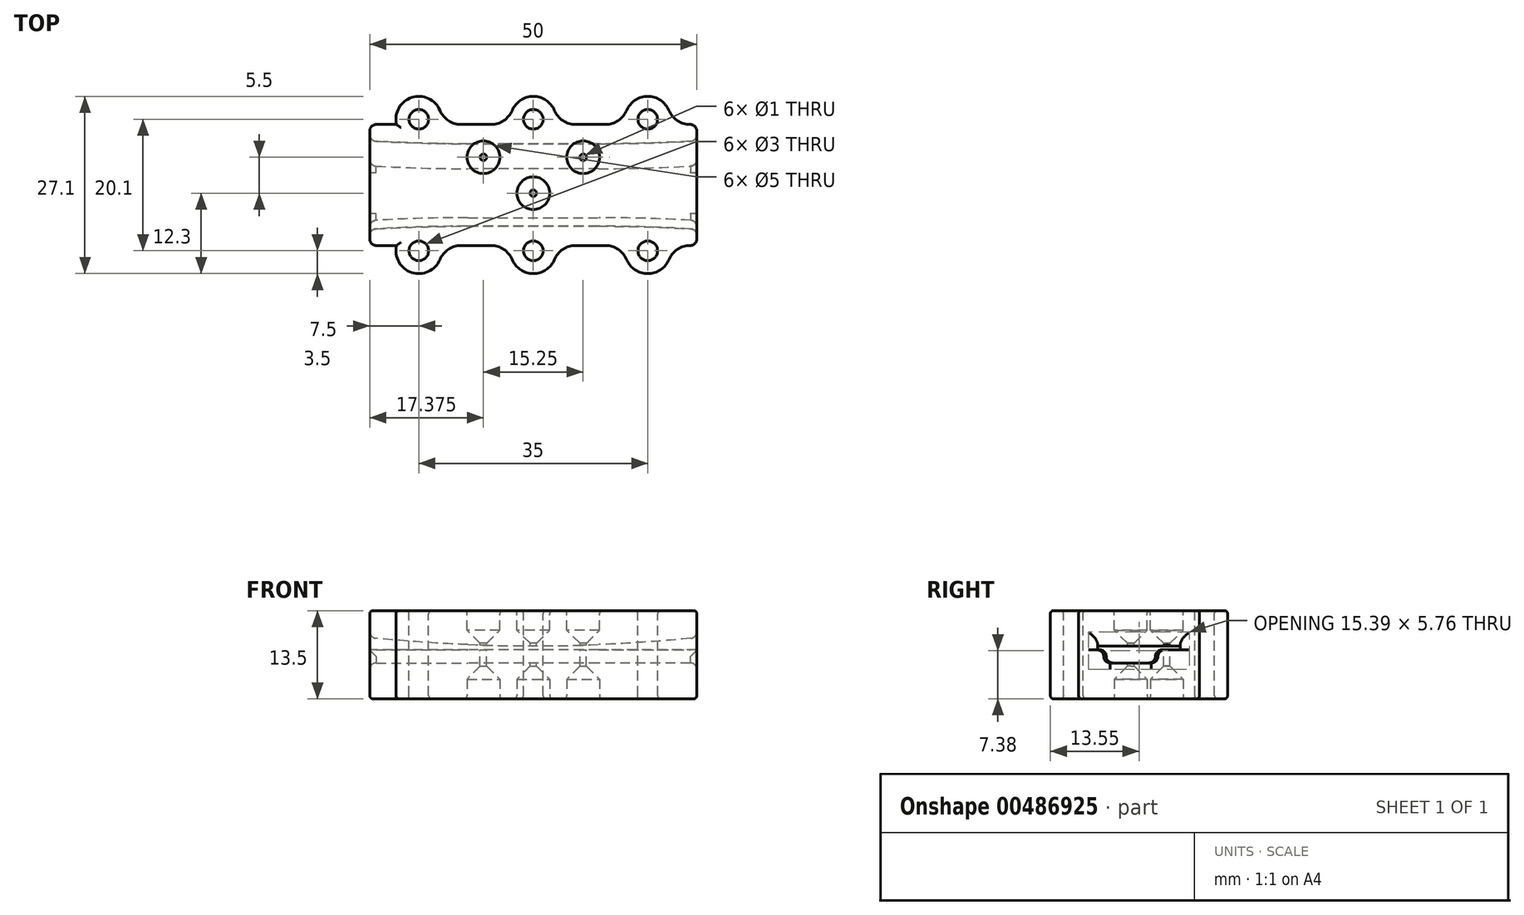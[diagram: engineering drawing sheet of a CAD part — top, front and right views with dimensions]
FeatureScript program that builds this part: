
annotation { "Feature Type Name" : "Feature", "Feature Type Description" : "" }
export const myFeature = defineFeature(function(context is Context, id is Id, definition is map)
    precondition{}
    {
        {
            var Q0;
            Q0=qCreatedBy(makeId("Top.planeOp"),FACE);
            var sketch = newSketch(context, id + "F0", { "sketchPlane" : qUnion([Q0])});
            skLineSegment(sketch, "E0", {"start": v(0, 5) * mm, "end": v(25, 5) * mm});
            skLineSegment(sketch, "E1", {"start": v(0, -4.25) * mm, "end": v(25, -4.25) * mm, "construction": true});
            skArc(sketch, "E2", {"start": v(10, 2.05) * mm, "mid": v(17.5, 2.16) * mm, "end": v(25, 2.5) * mm});
            skPoint(sketch, "E3", {"position": v(0, 2.25) * mm});
            skLineSegment(sketch, "E4", {"start": v(25, 5) * mm, "end": v(25, 2.5) * mm});
            skPoint(sketch, "E5", {"position": v(25, 2.5) * mm});
            skLineSegment(sketch, "E6.MirrorCS", {"start": v(0, 5) * mm, "end": v(-25, 5) * mm});
            skLineSegment(sketch, "E7.MirrorCS", {"start": v(-25, 5) * mm, "end": v(-25, 2.5) * mm});
            skLineSegment(sketch, "E8.MirrorCS", {"start": v(25, -13.5) * mm, "end": v(25, -11) * mm});
            skLineSegment(sketch, "E9.MirrorCS", {"start": v(0, -13.5) * mm, "end": v(25, -13.5) * mm});
            skLineSegment(sketch, "E10.MirrorCS", {"start": v(0, -13.5) * mm, "end": v(-25, -13.5) * mm});
            skLineSegment(sketch, "E11.MirrorCS", {"start": v(-25, -13.5) * mm, "end": v(-25, -11) * mm});
            skPoint(sketch, "E12", {"position": v(10, 2.05) * mm});
            skLineSegment(sketch, "E13", {"start": v(0, 2.05) * mm, "end": v(10, 2.05) * mm});
            skLineSegment(sketch, "E14.MirrorCS", {"start": v(0, 2.05) * mm, "end": v(-10, 2.05) * mm});
            skArc(sketch, "E15.MirrorCS", {"start": v(-10, 2.05) * mm, "mid": v(-17.5, 2.16) * mm, "end": v(-25, 2.5) * mm});
            skArc(sketch, "E16.MirrorCS", {"start": v(10, -10.55) * mm, "mid": v(17.5, -10.66) * mm, "end": v(25, -11) * mm});
            skLineSegment(sketch, "E17.MirrorCS", {"start": v(0, -10.55) * mm, "end": v(10, -10.55) * mm});
            skLineSegment(sketch, "E18.MirrorCS", {"start": v(0, -10.55) * mm, "end": v(-10, -10.55) * mm});
            skArc(sketch, "E19.MirrorCS", {"start": v(-10, -10.55) * mm, "mid": v(-17.5, -10.66) * mm, "end": v(-25, -11) * mm});
            skLineSegment(sketch, "E20", {"start": v(0, 1.75) * mm, "end": v(25, 1.75) * mm, "construction": true});
            skLineSegment(sketch, "E21", {"start": v(0, -10.25) * mm, "end": v(25, -10.25) * mm, "construction": true});
            skLineSegment(sketch, "E22", {"start": v(25, -10.25) * mm, "end": v(25, -4.25) * mm, "construction": true});
            skLineSegment(sketch, "E23", {"start": v(25, 1.75) * mm, "end": v(25, -4.25) * mm, "construction": true});
            skLineSegment(sketch, "E24", {"start": v(0, -5.5) * mm, "end": v(25, -5.5) * mm, "construction": true});
            skSolve(sketch);
        }
        {
            var Q0;
            Q0=makeQuery(id+"F0.imprint","IMPRINT",FACE,{"disambiguationData":[TD([[makeQuery(id+"F0.imprint","IMPRINT",EDGE,{"derivedFrom":sQuery(id+"F0.wireOp",EDGE,"E0")}),-1.0]])]});
            var Q1;
            Q1=makeQuery(id+"F0.imprint","IMPRINT",FACE,{"disambiguationData":[TD([[makeQuery(id+"F0.imprint","IMPRINT",EDGE,{"derivedFrom":sQuery(id+"F0.wireOp",EDGE,"E8.MirrorCS")}),1.0]])]});
            extrude(context, id + "F1", {"entities" : qUnion([Q0, Q1]), "depth" : 6 * mm});
        }
        {
            var Q0;
            Q0=makeQuery(id+"F1.opExtrude","SWEPT_FACE",FACE,{"disambiguationData":[OSD([sQuery(id+"F0.wireOp",EDGE,"E9.MirrorCS"),sQuery(id+"F0.wireOp",EDGE,"E10.MirrorCS")])]});
            var sketch = newSketch(context, id + "F2", { "sketchPlane" : qUnion([Q0])});
            skLineSegment(sketch, "E25", {"start": v(0, 6) * mm, "end": v(25, 6) * mm});
            skLineSegment(sketch, "E26", {"start": v(25, 6) * mm, "end": v(25, 1.85) * mm});
            skArc(sketch, "E27", {"start": v(0, 0.6) * mm, "mid": v(12.52, 0.91) * mm, "end": v(25, 1.85) * mm});
            skPoint(sketch, "E28", {"position": v(25, 1.85) * mm});
            skPoint(sketch, "E29", {"position": v(0, 0.6) * mm});
            skLineSegment(sketch, "E30.MirrorCS", {"start": v(0, 6) * mm, "end": v(-25, 6) * mm});
            skLineSegment(sketch, "E31.MirrorCS", {"start": v(-25, 6) * mm, "end": v(-25, 1.85) * mm});
            skArc(sketch, "E32.MirrorCS", {"start": v(0, 0.6) * mm, "mid": v(-12.52, 0.91) * mm, "end": v(-25, 1.85) * mm});
            skSolve(sketch);
        }
        {
            var Q0;
            Q0 = qSketchRegion(id + "F2", true);
            var Q1;
            Q1=makeQuery(id+"F1.opExtrude","SWEPT_FACE",FACE,{"disambiguationData":[OSD([sQuery(id+"F0.wireOp",EDGE,"E0"),sQuery(id+"F0.wireOp",EDGE,"9c2fb416-197e-4b27-b734-f3fda417422a0.MirrorCS")])]});
            extrude(context, id + "F3", {"entities" : qUnion([Q0]), "operationType" : NewBodyOperationType.ADD, "endBound" : BoundingType.UP_TO_SURFACE, "oppositeDirection" : true, "endBoundEntityFace" : qUnion([Q1]), "depth" : 25 * mm});
        }
        {
            var Q0;
            Q0=makeQuery(id+"F1.opExtrude","CAP_FACE",FACE,{"disambiguationData":[OSD([sQuery(id+"F0.wireOp",EDGE,"E8.MirrorCS"),sQuery(id+"F0.wireOp",EDGE,"E9.MirrorCS"),sQuery(id+"F0.wireOp",EDGE,"E10.MirrorCS"),sQuery(id+"F0.wireOp",EDGE,"E11.MirrorCS"),sQuery(id+"F0.wireOp",EDGE,"E16.MirrorCS"),sQuery(id+"F0.wireOp",EDGE,"E17.MirrorCS"),sQuery(id+"F0.wireOp",EDGE,"E18.MirrorCS"),sQuery(id+"F0.wireOp",EDGE,"E19.MirrorCS")])],"isStart":true});
            var sketch = newSketch(context, id + "F4", { "sketchPlane" : qUnion([Q0])});
            skLineSegment(sketch, "E33", {"start": v(-10, 9.25) * mm, "end": v(10, 9.25) * mm});
            skLineSegment(sketch, "E34", {"start": v(-25, 13.5) * mm, "end": v(25, 13.5) * mm});
            skArc(sketch, "E35", {"start": v(-25, 9.7) * mm, "mid": v(-17.5, 9.36) * mm, "end": v(-10, 9.25) * mm});
            skLineSegment(sketch, "E36", {"start": v(-25, 13.5) * mm, "end": v(-25, 9.7) * mm});
            skArc(sketch, "E37.MirrorCS", {"start": v(25, 9.7) * mm, "mid": v(17.5, 9.36) * mm, "end": v(10, 9.25) * mm});
            skLineSegment(sketch, "E38.MirrorCS", {"start": v(25, 13.5) * mm, "end": v(25, 9.7) * mm});
            skLineSegment(sketch, "E39", {"start": v(-25, 1.3) * mm, "end": v(-25, -5) * mm});
            skLineSegment(sketch, "E40", {"start": v(-25, -5) * mm, "end": v(25, -5) * mm});
            skLineSegment(sketch, "E41", {"start": v(25, -5) * mm, "end": v(25, 1.3) * mm});
            skArc(sketch, "E42.MirrorCS", {"start": v(25, 1.3) * mm, "mid": v(17.5, 1.64) * mm, "end": v(10, 1.75) * mm});
            skLineSegment(sketch, "E43.MirrorCS", {"start": v(-10, 1.75) * mm, "end": v(10, 1.75) * mm});
            skArc(sketch, "E44.MirrorCS", {"start": v(-25, 1.3) * mm, "mid": v(-17.5, 1.64) * mm, "end": v(-10, 1.75) * mm});
            skSolve(sketch);
        }
        {
            var Q0;
            Q0 = qSketchRegion(id + "F4", true);
            extrude(context, id + "F5", {"entities" : qUnion([Q0]), "depth" : 7.5 * mm});
        }
        {
            var Q0;
            Q0=makeQuery(id+"F5.opExtrude","SWEPT_FACE",FACE,{"disambiguationData":[OSD([sQuery(id+"F4.wireOp",EDGE,"E34")])]});
            var sketch = newSketch(context, id + "F6", { "sketchPlane" : qUnion([Q0])});
            skPoint(sketch, "E45", {"position": v(-25, -2) * mm});
            skPoint(sketch, "E46", {"position": v(25, -2) * mm});
            skLineSegment(sketch, "E47", {"start": v(-25, -2) * mm, "end": v(-25, -7.5) * mm});
            skLineSegment(sketch, "E48", {"start": v(-25, -7.5) * mm, "end": v(25, -7.5) * mm});
            skLineSegment(sketch, "E49", {"start": v(25, -7.5) * mm, "end": v(25, -2) * mm});
            skLineSegment(sketch, "E50", {"start": v(25, -2) * mm, "end": v(-25, -2) * mm});
            skSolve(sketch);
        }
        {
            var Q0;
            Q0 = qSketchRegion(id + "F6", true);
            var Q1;
            Q1=makeQuery(id+"F5.opExtrude","SWEPT_FACE",FACE,{"disambiguationData":[OSD([sQuery(id+"F4.wireOp",EDGE,"E40")])]});
            extrude(context, id + "F7", {"entities" : qUnion([Q0]), "operationType" : NewBodyOperationType.ADD, "endBound" : BoundingType.UP_TO_SURFACE, "oppositeDirection" : true, "endBoundEntityFace" : qUnion([Q1]), "depth" : 25 * mm});
        }
        {
            var Q0;
            Q0=makeQuery(id+"F3.boolean.opBoolean","MERGE",FACE,{"derivedFrom":[makeQuery(id+"F1.opExtrude","CAP_FACE",FACE,{"disambiguationData":[OSD([sQuery(id+"F0.wireOp",EDGE,"E0"),sQuery(id+"F0.wireOp",EDGE,"E2"),sQuery(id+"F0.wireOp",EDGE,"E4"),sQuery(id+"F0.wireOp",EDGE,"E6.MirrorCS"),sQuery(id+"F0.wireOp",EDGE,"E7.MirrorCS"),sQuery(id+"F0.wireOp",EDGE,"E13"),sQuery(id+"F0.wireOp",EDGE,"E14.MirrorCS"),sQuery(id+"F0.wireOp",EDGE,"E15.MirrorCS")])],"isStart":false}),makeQuery(id+"F1.opExtrude","CAP_FACE",FACE,{"disambiguationData":[OSD([sQuery(id+"F0.wireOp",EDGE,"E8.MirrorCS"),sQuery(id+"F0.wireOp",EDGE,"E9.MirrorCS"),sQuery(id+"F0.wireOp",EDGE,"E10.MirrorCS"),sQuery(id+"F0.wireOp",EDGE,"E11.MirrorCS"),sQuery(id+"F0.wireOp",EDGE,"E16.MirrorCS"),sQuery(id+"F0.wireOp",EDGE,"E17.MirrorCS"),sQuery(id+"F0.wireOp",EDGE,"E18.MirrorCS"),sQuery(id+"F0.wireOp",EDGE,"E19.MirrorCS")])],"isStart":false}),makeQuery(id+"F3.opExtrude","SWEPT_FACE",FACE,{"disambiguationData":[OSD([sQuery(id+"F2.wireOp",EDGE,"E25"),sQuery(id+"F2.wireOp",EDGE,"E30.MirrorCS")])]})]});
            var sketch = newSketch(context, id + "F8", { "sketchPlane" : qUnion([Q0])});
            skArc(sketch, "E51", {"start": v(14.1, -13.5) * mm, "mid": v(17.5, -17.8) * mm, "end": v(20.9, -13.5) * mm});
            skArc(sketch, "E52", {"start": v(20.9, 5) * mm, "mid": v(17.5, 9.3) * mm, "end": v(14.1, 5) * mm});
            skLineSegment(sketch, "E53", {"start": v(20.9, -13.5) * mm, "end": v(14.1, -13.5) * mm});
            skLineSegment(sketch, "E54", {"start": v(20.9, 5) * mm, "end": v(14.1, 5) * mm});
            skArc(sketch, "E55.MirrorCS", {"start": v(-14.1, -13.5) * mm, "mid": v(-17.5, -17.8) * mm, "end": v(-20.9, -13.5) * mm});
            skArc(sketch, "E56.MirrorCS", {"start": v(-20.9, 5) * mm, "mid": v(-17.5, 9.3) * mm, "end": v(-14.1, 5) * mm});
            skLineSegment(sketch, "E57.MirrorCS", {"start": v(-20.9, 5) * mm, "end": v(-14.1, 5) * mm});
            skLineSegment(sketch, "E58.MirrorCS", {"start": v(-20.9, -13.5) * mm, "end": v(-14.1, -13.5) * mm});
            skArc(sketch, "E59", {"start": v(3.4, 5) * mm, "mid": v(0, 9.3) * mm, "end": v(-3.4, 5) * mm});
            skArc(sketch, "E60", {"start": v(-3.4, -13.5) * mm, "mid": v(0, -17.8) * mm, "end": v(3.4, -13.5) * mm});
            skLineSegment(sketch, "E61", {"start": v(-3.4, 5) * mm, "end": v(3.4, 5) * mm});
            skLineSegment(sketch, "E62", {"start": v(-3.4, -13.5) * mm, "end": v(3.4, -13.5) * mm});
            skSolve(sketch);
        }
        {
            var Q0;
            Q0 = qSketchRegion(id + "F8", true);
            var Q1;
            Q1=makeQuery(id+"F1.opExtrude","CAP_FACE",FACE,{"disambiguationData":[OSD([sQuery(id+"F0.wireOp",EDGE,"E8.MirrorCS"),sQuery(id+"F0.wireOp",EDGE,"E9.MirrorCS"),sQuery(id+"F0.wireOp",EDGE,"E10.MirrorCS"),sQuery(id+"F0.wireOp",EDGE,"E11.MirrorCS"),sQuery(id+"F0.wireOp",EDGE,"E16.MirrorCS"),sQuery(id+"F0.wireOp",EDGE,"E17.MirrorCS"),sQuery(id+"F0.wireOp",EDGE,"E18.MirrorCS"),sQuery(id+"F0.wireOp",EDGE,"E19.MirrorCS")])],"isStart":true});
            extrude(context, id + "F9", {"entities" : qUnion([Q0]), "operationType" : NewBodyOperationType.ADD, "endBound" : BoundingType.UP_TO_SURFACE, "oppositeDirection" : true, "endBoundEntityFace" : qUnion([Q1]), "depth" : 25 * mm});
        }
        {
            var Q0;
            Q0=makeQuery(id+"F7.boolean.opBoolean","MERGE",FACE,{"derivedFrom":[makeQuery(id+"F5.opExtrude","CAP_FACE",FACE,{"disambiguationData":[OSD([sQuery(id+"F4.wireOp",EDGE,"E33"),sQuery(id+"F4.wireOp",EDGE,"E34"),sQuery(id+"F4.wireOp",EDGE,"E35"),sQuery(id+"F4.wireOp",EDGE,"E36"),sQuery(id+"F4.wireOp",EDGE,"E37.MirrorCS"),sQuery(id+"F4.wireOp",EDGE,"E38.MirrorCS")])],"isStart":false}),makeQuery(id+"F5.opExtrude","CAP_FACE",FACE,{"disambiguationData":[OSD([sQuery(id+"F4.wireOp",EDGE,"E39"),sQuery(id+"F4.wireOp",EDGE,"E40"),sQuery(id+"F4.wireOp",EDGE,"E41"),sQuery(id+"F4.wireOp",EDGE,"E42.MirrorCS"),sQuery(id+"F4.wireOp",EDGE,"E43.MirrorCS"),sQuery(id+"F4.wireOp",EDGE,"E44.MirrorCS")])],"isStart":false}),makeQuery(id+"F7.opExtrude","SWEPT_FACE",FACE,{"disambiguationData":[OSD([sQuery(id+"F6.wireOp",EDGE,"E48")])]})]});
            var sketch = newSketch(context, id + "F10", { "sketchPlane" : qUnion([Q0])});
            skArc(sketch, "E63", {"start": v(-14.1, 13.5) * mm, "mid": v(-17.5, 17.8) * mm, "end": v(-20.9, 13.5) * mm});
            skArc(sketch, "E64", {"start": v(-20.9, -5) * mm, "mid": v(-17.5, -9.3) * mm, "end": v(-14.1, -5) * mm});
            skLineSegment(sketch, "E65", {"start": v(-20.9, 13.5) * mm, "end": v(-14.1, 13.5) * mm});
            skLineSegment(sketch, "E66", {"start": v(-20.9, -5) * mm, "end": v(-14.1, -5) * mm});
            skArc(sketch, "E67.MirrorCS", {"start": v(14.1, 13.5) * mm, "mid": v(17.5, 17.8) * mm, "end": v(20.9, 13.5) * mm});
            skLineSegment(sketch, "E68.MirrorCS", {"start": v(20.9, 13.5) * mm, "end": v(14.1, 13.5) * mm});
            skLineSegment(sketch, "E69.MirrorCS", {"start": v(20.9, -5) * mm, "end": v(14.1, -5) * mm});
            skArc(sketch, "E70.MirrorCS", {"start": v(20.9, -5) * mm, "mid": v(17.5, -9.3) * mm, "end": v(14.1, -5) * mm});
            skArc(sketch, "E71", {"start": v(-3.4, -5) * mm, "mid": v(0, -9.3) * mm, "end": v(3.4, -5) * mm});
            skArc(sketch, "E72", {"start": v(3.4, 13.5) * mm, "mid": v(0, 17.8) * mm, "end": v(-3.4, 13.5) * mm});
            skLineSegment(sketch, "E73", {"start": v(3.4, -5) * mm, "end": v(-3.4, -5) * mm});
            skLineSegment(sketch, "E74", {"start": v(3.4, 13.5) * mm, "end": v(-3.4, 13.5) * mm});
            skSolve(sketch);
        }
        {
            var Q0;
            Q0 = qSketchRegion(id + "F10", true);
            var Q1;
            Q1=makeQuery(id+"F5.opExtrude","CAP_FACE",FACE,{"disambiguationData":[OSD([sQuery(id+"F4.wireOp",EDGE,"E33"),sQuery(id+"F4.wireOp",EDGE,"E34"),sQuery(id+"F4.wireOp",EDGE,"E35"),sQuery(id+"F4.wireOp",EDGE,"E36"),sQuery(id+"F4.wireOp",EDGE,"E37.MirrorCS"),sQuery(id+"F4.wireOp",EDGE,"E38.MirrorCS")])],"isStart":true});
            extrude(context, id + "F11", {"entities" : qUnion([Q0]), "operationType" : NewBodyOperationType.ADD, "endBound" : BoundingType.UP_TO_SURFACE, "oppositeDirection" : true, "endBoundEntityFace" : qUnion([Q1]), "depth" : 25 * mm});
        }
        {
            var Q0;
            Q0=makeQuery(id+"F9.boolean.opBoolean","MERGE",FACE,{"derivedFrom":[makeQuery(id+"F3.boolean.opBoolean","MERGE",FACE,{"derivedFrom":[makeQuery(id+"F1.opExtrude","CAP_FACE",FACE,{"disambiguationData":[OSD([sQuery(id+"F0.wireOp",EDGE,"E0"),sQuery(id+"F0.wireOp",EDGE,"E2"),sQuery(id+"F0.wireOp",EDGE,"E4"),sQuery(id+"F0.wireOp",EDGE,"E6.MirrorCS"),sQuery(id+"F0.wireOp",EDGE,"E7.MirrorCS"),sQuery(id+"F0.wireOp",EDGE,"E13"),sQuery(id+"F0.wireOp",EDGE,"E14.MirrorCS"),sQuery(id+"F0.wireOp",EDGE,"E15.MirrorCS")])],"isStart":false}),makeQuery(id+"F1.opExtrude","CAP_FACE",FACE,{"disambiguationData":[OSD([sQuery(id+"F0.wireOp",EDGE,"E8.MirrorCS"),sQuery(id+"F0.wireOp",EDGE,"E9.MirrorCS"),sQuery(id+"F0.wireOp",EDGE,"E10.MirrorCS"),sQuery(id+"F0.wireOp",EDGE,"E11.MirrorCS"),sQuery(id+"F0.wireOp",EDGE,"E16.MirrorCS"),sQuery(id+"F0.wireOp",EDGE,"E17.MirrorCS"),sQuery(id+"F0.wireOp",EDGE,"E18.MirrorCS"),sQuery(id+"F0.wireOp",EDGE,"E19.MirrorCS")])],"isStart":false}),makeQuery(id+"F3.opExtrude","SWEPT_FACE",FACE,{"disambiguationData":[OSD([sQuery(id+"F2.wireOp",EDGE,"E25"),sQuery(id+"F2.wireOp",EDGE,"E30.MirrorCS")])]})]}),makeQuery(id+"F9.opExtrude","CAP_FACE",FACE,{"disambiguationData":[OSD([sQuery(id+"F8.wireOp",EDGE,"E51"),sQuery(id+"F8.wireOp",EDGE,"E53")])],"isStart":true}),makeQuery(id+"F9.opExtrude","CAP_FACE",FACE,{"disambiguationData":[OSD([sQuery(id+"F8.wireOp",EDGE,"E52"),sQuery(id+"F8.wireOp",EDGE,"E54")])],"isStart":true}),makeQuery(id+"F9.opExtrude","CAP_FACE",FACE,{"disambiguationData":[OSD([sQuery(id+"F8.wireOp",EDGE,"E55.MirrorCS"),sQuery(id+"F8.wireOp",EDGE,"E58.MirrorCS")])],"isStart":true}),makeQuery(id+"F9.opExtrude","CAP_FACE",FACE,{"disambiguationData":[OSD([sQuery(id+"F8.wireOp",EDGE,"E56.MirrorCS"),sQuery(id+"F8.wireOp",EDGE,"E57.MirrorCS")])],"isStart":true}),makeQuery(id+"F9.opExtrude","CAP_FACE",FACE,{"disambiguationData":[OSD([sQuery(id+"F8.wireOp",EDGE,"E59"),sQuery(id+"F8.wireOp",EDGE,"E61")])],"isStart":true}),makeQuery(id+"F9.opExtrude","CAP_FACE",FACE,{"disambiguationData":[OSD([sQuery(id+"F8.wireOp",EDGE,"E60"),sQuery(id+"F8.wireOp",EDGE,"E62")])],"isStart":true})]});
            var sketch = newSketch(context, id + "F12", { "sketchPlane" : qUnion([Q0])});
            skCircle(sketch, "E75", {"center": v(-7.62, 0) * mm, "radius": 0.5 * mm});
            skCircle(sketch, "E76.MirrorC", {"center": v(7.62, 0) * mm, "radius": 0.5 * mm});
            skCircle(sketch, "E77", {"center": v(0, -5.5) * mm, "radius": 0.5 * mm});
            skCircle(sketch, "E78", {"center": v(-17.5, 5.8) * mm, "radius": 1.5 * mm});
            skCircle(sketch, "E79", {"center": v(-17.5, -14.3) * mm, "radius": 1.5 * mm});
            skCircle(sketch, "E80.MirrorC", {"center": v(17.5, -14.3) * mm, "radius": 1.5 * mm});
            skCircle(sketch, "E81.MirrorC", {"center": v(17.5, 5.8) * mm, "radius": 1.5 * mm});
            skCircle(sketch, "E82", {"center": v(0, 5.8) * mm, "radius": 1.5 * mm});
            skCircle(sketch, "E83", {"center": v(0, -14.3) * mm, "radius": 1.5 * mm});
            skSolve(sketch);
        }
        {
            var Q0;
            Q0 = qSketchRegion(id + "F12", true);
            extrude(context, id + "F13", {"entities" : qUnion([Q0]), "operationType" : NewBodyOperationType.REMOVE, "endBound" : BoundingType.THROUGH_ALL, "oppositeDirection" : true, "depth" : 25 * mm});
        }
        {
            var Q0;
            Q0=makeQuery(id+"F9.boolean.opBoolean","MERGE",FACE,{"derivedFrom":[makeQuery(id+"F3.boolean.opBoolean","MERGE",FACE,{"derivedFrom":[makeQuery(id+"F1.opExtrude","CAP_FACE",FACE,{"disambiguationData":[OSD([sQuery(id+"F0.wireOp",EDGE,"E0"),sQuery(id+"F0.wireOp",EDGE,"E2"),sQuery(id+"F0.wireOp",EDGE,"E4"),sQuery(id+"F0.wireOp",EDGE,"E6.MirrorCS"),sQuery(id+"F0.wireOp",EDGE,"E7.MirrorCS"),sQuery(id+"F0.wireOp",EDGE,"E13"),sQuery(id+"F0.wireOp",EDGE,"E14.MirrorCS"),sQuery(id+"F0.wireOp",EDGE,"E15.MirrorCS")])],"isStart":false}),makeQuery(id+"F1.opExtrude","CAP_FACE",FACE,{"disambiguationData":[OSD([sQuery(id+"F0.wireOp",EDGE,"E8.MirrorCS"),sQuery(id+"F0.wireOp",EDGE,"E9.MirrorCS"),sQuery(id+"F0.wireOp",EDGE,"E10.MirrorCS"),sQuery(id+"F0.wireOp",EDGE,"E11.MirrorCS"),sQuery(id+"F0.wireOp",EDGE,"E16.MirrorCS"),sQuery(id+"F0.wireOp",EDGE,"E17.MirrorCS"),sQuery(id+"F0.wireOp",EDGE,"E18.MirrorCS"),sQuery(id+"F0.wireOp",EDGE,"E19.MirrorCS")])],"isStart":false}),makeQuery(id+"F3.opExtrude","SWEPT_FACE",FACE,{"disambiguationData":[OSD([sQuery(id+"F2.wireOp",EDGE,"E25"),sQuery(id+"F2.wireOp",EDGE,"E30.MirrorCS")])]})]}),makeQuery(id+"F9.opExtrude","CAP_FACE",FACE,{"disambiguationData":[OSD([sQuery(id+"F8.wireOp",EDGE,"E51"),sQuery(id+"F8.wireOp",EDGE,"E53")])],"isStart":true}),makeQuery(id+"F9.opExtrude","CAP_FACE",FACE,{"disambiguationData":[OSD([sQuery(id+"F8.wireOp",EDGE,"E52"),sQuery(id+"F8.wireOp",EDGE,"E54")])],"isStart":true}),makeQuery(id+"F9.opExtrude","CAP_FACE",FACE,{"disambiguationData":[OSD([sQuery(id+"F8.wireOp",EDGE,"E55.MirrorCS"),sQuery(id+"F8.wireOp",EDGE,"E58.MirrorCS")])],"isStart":true}),makeQuery(id+"F9.opExtrude","CAP_FACE",FACE,{"disambiguationData":[OSD([sQuery(id+"F8.wireOp",EDGE,"E56.MirrorCS"),sQuery(id+"F8.wireOp",EDGE,"E57.MirrorCS")])],"isStart":true}),makeQuery(id+"F9.opExtrude","CAP_FACE",FACE,{"disambiguationData":[OSD([sQuery(id+"F8.wireOp",EDGE,"E59"),sQuery(id+"F8.wireOp",EDGE,"E61")])],"isStart":true}),makeQuery(id+"F9.opExtrude","CAP_FACE",FACE,{"disambiguationData":[OSD([sQuery(id+"F8.wireOp",EDGE,"E60"),sQuery(id+"F8.wireOp",EDGE,"E62")])],"isStart":true})]});
            var sketch = newSketch(context, id + "F14", { "sketchPlane" : qUnion([Q0])});
            skCircle(sketch, "E84", {"center": v(-7.62, 0) * mm, "radius": 2.5 * mm});
            skCircle(sketch, "E85", {"center": v(7.62, 0) * mm, "radius": 2.5 * mm});
            skCircle(sketch, "E86", {"center": v(0, -5.5) * mm, "radius": 2.5 * mm});
            skSolve(sketch);
        }
        {
            var Q0;
            Q0 = qSketchRegion(id + "F14", true);
            extrude(context, id + "F15", {"entities" : qUnion([Q0]), "operationType" : NewBodyOperationType.REMOVE, "oppositeDirection" : true, "depth" : 5 * mm});
        }
        {
            var Q0;
            Q0=makeQuery(id+"F11.boolean.opBoolean","MERGE",FACE,{"derivedFrom":[makeQuery(id+"F7.boolean.opBoolean","MERGE",FACE,{"derivedFrom":[makeQuery(id+"F5.opExtrude","CAP_FACE",FACE,{"disambiguationData":[OSD([sQuery(id+"F4.wireOp",EDGE,"E33"),sQuery(id+"F4.wireOp",EDGE,"E34"),sQuery(id+"F4.wireOp",EDGE,"E35"),sQuery(id+"F4.wireOp",EDGE,"E36"),sQuery(id+"F4.wireOp",EDGE,"E37.MirrorCS"),sQuery(id+"F4.wireOp",EDGE,"E38.MirrorCS")])],"isStart":false}),makeQuery(id+"F5.opExtrude","CAP_FACE",FACE,{"disambiguationData":[OSD([sQuery(id+"F4.wireOp",EDGE,"E39"),sQuery(id+"F4.wireOp",EDGE,"E40"),sQuery(id+"F4.wireOp",EDGE,"E41"),sQuery(id+"F4.wireOp",EDGE,"E42.MirrorCS"),sQuery(id+"F4.wireOp",EDGE,"E43.MirrorCS"),sQuery(id+"F4.wireOp",EDGE,"E44.MirrorCS")])],"isStart":false}),makeQuery(id+"F7.opExtrude","SWEPT_FACE",FACE,{"disambiguationData":[OSD([sQuery(id+"F6.wireOp",EDGE,"E48")])]})]}),makeQuery(id+"F11.opExtrude","CAP_FACE",FACE,{"disambiguationData":[OSD([sQuery(id+"F10.wireOp",EDGE,"E63"),sQuery(id+"F10.wireOp",EDGE,"E65")])],"isStart":true}),makeQuery(id+"F11.opExtrude","CAP_FACE",FACE,{"disambiguationData":[OSD([sQuery(id+"F10.wireOp",EDGE,"E64"),sQuery(id+"F10.wireOp",EDGE,"E66")])],"isStart":true}),makeQuery(id+"F11.opExtrude","CAP_FACE",FACE,{"disambiguationData":[OSD([sQuery(id+"F10.wireOp",EDGE,"E67.MirrorCS"),sQuery(id+"F10.wireOp",EDGE,"E68.MirrorCS")])],"isStart":true}),makeQuery(id+"F11.opExtrude","CAP_FACE",FACE,{"disambiguationData":[OSD([sQuery(id+"F10.wireOp",EDGE,"E69.MirrorCS"),sQuery(id+"F10.wireOp",EDGE,"E70.MirrorCS")])],"isStart":true}),makeQuery(id+"F11.opExtrude","CAP_FACE",FACE,{"disambiguationData":[OSD([sQuery(id+"F10.wireOp",EDGE,"E71"),sQuery(id+"F10.wireOp",EDGE,"E73")])],"isStart":true}),makeQuery(id+"F11.opExtrude","CAP_FACE",FACE,{"disambiguationData":[OSD([sQuery(id+"F10.wireOp",EDGE,"E72"),sQuery(id+"F10.wireOp",EDGE,"E74")])],"isStart":true})]});
            var sketch = newSketch(context, id + "F16", { "sketchPlane" : qUnion([Q0])});
            skCircle(sketch, "E87", {"center": v(7.62, 0) * mm, "radius": 2.5 * mm});
            skCircle(sketch, "E88", {"center": v(-7.62, 0) * mm, "radius": 2.5 * mm});
            skCircle(sketch, "E89", {"center": v(0, 5.5) * mm, "radius": 2.5 * mm});
            skSolve(sketch);
        }
        {
            var Q0;
            Q0 = qSketchRegion(id + "F16", true);
            extrude(context, id + "F17", {"entities" : qUnion([Q0]), "operationType" : NewBodyOperationType.REMOVE, "oppositeDirection" : true, "depth" : 5 * mm});
        }
        {
            var Q0;
            Q0=makeQuery(id+"F15.boolean.opBoolean","COPY",EDGE,{"derivedFrom":makeQuery(id+"F15.opExtrude","CAP_EDGE",EDGE,{"disambiguationData":[OSD([sQuery(id+"F14.wireOp",EDGE,"E85")])],"isStart":false})});
            var Q1;
            Q1=makeQuery(id+"F15.boolean.opBoolean","COPY",EDGE,{"derivedFrom":makeQuery(id+"F15.opExtrude","CAP_EDGE",EDGE,{"disambiguationData":[OSD([sQuery(id+"F14.wireOp",EDGE,"E86")])],"isStart":false})});
            var Q2;
            Q2=makeQuery(id+"F15.boolean.opBoolean","COPY",EDGE,{"derivedFrom":makeQuery(id+"F15.opExtrude","CAP_EDGE",EDGE,{"disambiguationData":[OSD([sQuery(id+"F14.wireOp",EDGE,"E84")])],"isStart":false})});
            var Q3;
            Q3=makeQuery(id+"F17.boolean.opBoolean","COPY",EDGE,{"derivedFrom":makeQuery(id+"F17.opExtrude","CAP_EDGE",EDGE,{"disambiguationData":[OSD([sQuery(id+"F16.wireOp",EDGE,"E87")])],"isStart":false})});
            var Q4;
            Q4=makeQuery(id+"F17.boolean.opBoolean","COPY",EDGE,{"derivedFrom":makeQuery(id+"F17.opExtrude","CAP_EDGE",EDGE,{"disambiguationData":[OSD([sQuery(id+"F16.wireOp",EDGE,"E88")])],"isStart":false})});
            var Q5;
            Q5=makeQuery(id+"F17.boolean.opBoolean","COPY",EDGE,{"derivedFrom":makeQuery(id+"F17.opExtrude","CAP_EDGE",EDGE,{"disambiguationData":[OSD([sQuery(id+"F16.wireOp",EDGE,"E89")])],"isStart":false})});
            chamfer(context, id + "F18", {"entities" : qUnion([Q0, Q1, Q2, Q3, Q4, Q5]), "width" : 2 * mm, "tangentPropagation" : true});
        }
        {
            var Q0;
            {var subQ0=sQuery(id+"F8.wireOp",EDGE,"E54");var subQ1=sQuery(id+"F8.wireOp",EDGE,"E52");var subQ2=sQuery(id+"F0.wireOp",EDGE,"E6.MirrorCS");var subQ3=sQuery(id+"F0.wireOp",EDGE,"E0");Q0=makeQuery(id+"F9.opExtrude","SWEPT_EDGE",EDGE,{"disambiguationData":[OSD([subQ3,subQ2,subQ1,subQ0]),TDD([makeQuery(id+"F8.imprint","INTERSECT",VERTEX,{"disambiguationData":[OD(1.0)],"derivedFrom":[makeQuery(id+"F1.opExtrude","CAP_EDGE",EDGE,{"disambiguationData":[OSD([subQ3,subQ2])],"isStart":false}),subQ1,subQ0]})])]});}
            var Q1;
            {var subQ0=sQuery(id+"F8.wireOp",EDGE,"E57.MirrorCS");var subQ1=sQuery(id+"F8.wireOp",EDGE,"E56.MirrorCS");var subQ2=sQuery(id+"F0.wireOp",EDGE,"E6.MirrorCS");var subQ3=sQuery(id+"F0.wireOp",EDGE,"E0");Q1=makeQuery(id+"F9.opExtrude","SWEPT_EDGE",EDGE,{"disambiguationData":[OSD([subQ3,subQ2,subQ1,subQ0]),TDD([makeQuery(id+"F8.imprint","INTERSECT",VERTEX,{"disambiguationData":[OD(1.0)],"derivedFrom":[makeQuery(id+"F1.opExtrude","CAP_EDGE",EDGE,{"disambiguationData":[OSD([subQ3,subQ2])],"isStart":false}),subQ1,subQ0]})])]});}
            var Q2;
            {var subQ0=sQuery(id+"F8.wireOp",EDGE,"E54");var subQ1=sQuery(id+"F8.wireOp",EDGE,"E52");var subQ2=sQuery(id+"F0.wireOp",EDGE,"E6.MirrorCS");var subQ3=sQuery(id+"F0.wireOp",EDGE,"E0");Q2=makeQuery(id+"F9.opExtrude","SWEPT_EDGE",EDGE,{"disambiguationData":[OSD([subQ3,subQ2,subQ1,subQ0]),TDD([makeQuery(id+"F8.imprint","INTERSECT",VERTEX,{"disambiguationData":[OD(0.0)],"derivedFrom":[makeQuery(id+"F1.opExtrude","CAP_EDGE",EDGE,{"disambiguationData":[OSD([subQ3,subQ2])],"isStart":false}),subQ1,subQ0]})])]});}
            var Q3;
            {var subQ0=sQuery(id+"F8.wireOp",EDGE,"E57.MirrorCS");var subQ1=sQuery(id+"F8.wireOp",EDGE,"E56.MirrorCS");var subQ2=sQuery(id+"F0.wireOp",EDGE,"E6.MirrorCS");var subQ3=sQuery(id+"F0.wireOp",EDGE,"E0");Q3=makeQuery(id+"F9.opExtrude","SWEPT_EDGE",EDGE,{"disambiguationData":[OSD([subQ3,subQ2,subQ1,subQ0]),TDD([makeQuery(id+"F8.imprint","INTERSECT",VERTEX,{"disambiguationData":[OD(0.0)],"derivedFrom":[makeQuery(id+"F1.opExtrude","CAP_EDGE",EDGE,{"disambiguationData":[OSD([subQ3,subQ2])],"isStart":false}),subQ1,subQ0]})])]});}
            var Q4;
            {var subQ0=sQuery(id+"F8.wireOp",EDGE,"E58.MirrorCS");var subQ1=sQuery(id+"F8.wireOp",EDGE,"E55.MirrorCS");var subQ2=sQuery(id+"F0.wireOp",EDGE,"E10.MirrorCS");var subQ3=sQuery(id+"F0.wireOp",EDGE,"E9.MirrorCS");Q4=makeQuery(id+"F9.opExtrude","SWEPT_EDGE",EDGE,{"disambiguationData":[OSD([subQ3,subQ2,subQ1,subQ0]),TDD([makeQuery(id+"F8.imprint","INTERSECT",VERTEX,{"disambiguationData":[OD(1.0)],"derivedFrom":[makeQuery(id+"F1.opExtrude","CAP_EDGE",EDGE,{"disambiguationData":[OSD([subQ3,subQ2])],"isStart":false}),subQ1,subQ0]})])]});}
            var Q5;
            {var subQ0=sQuery(id+"F8.wireOp",EDGE,"E53");var subQ1=sQuery(id+"F8.wireOp",EDGE,"E51");var subQ2=sQuery(id+"F0.wireOp",EDGE,"E10.MirrorCS");var subQ3=sQuery(id+"F0.wireOp",EDGE,"E9.MirrorCS");Q5=makeQuery(id+"F9.opExtrude","SWEPT_EDGE",EDGE,{"disambiguationData":[OSD([subQ3,subQ2,subQ1,subQ0]),TDD([makeQuery(id+"F8.imprint","INTERSECT",VERTEX,{"disambiguationData":[OD(0.0)],"derivedFrom":[makeQuery(id+"F1.opExtrude","CAP_EDGE",EDGE,{"disambiguationData":[OSD([subQ3,subQ2])],"isStart":false}),subQ1,subQ0]})])]});}
            var Q6;
            {var subQ0=sQuery(id+"F8.wireOp",EDGE,"E53");var subQ1=sQuery(id+"F8.wireOp",EDGE,"E51");var subQ2=sQuery(id+"F0.wireOp",EDGE,"E10.MirrorCS");var subQ3=sQuery(id+"F0.wireOp",EDGE,"E9.MirrorCS");Q6=makeQuery(id+"F9.opExtrude","SWEPT_EDGE",EDGE,{"disambiguationData":[OSD([subQ3,subQ2,subQ1,subQ0]),TDD([makeQuery(id+"F8.imprint","INTERSECT",VERTEX,{"disambiguationData":[OD(1.0)],"derivedFrom":[makeQuery(id+"F1.opExtrude","CAP_EDGE",EDGE,{"disambiguationData":[OSD([subQ3,subQ2])],"isStart":false}),subQ1,subQ0]})])]});}
            var Q7;
            {var subQ0=sQuery(id+"F8.wireOp",EDGE,"E58.MirrorCS");var subQ1=sQuery(id+"F8.wireOp",EDGE,"E55.MirrorCS");var subQ2=sQuery(id+"F0.wireOp",EDGE,"E10.MirrorCS");var subQ3=sQuery(id+"F0.wireOp",EDGE,"E9.MirrorCS");Q7=makeQuery(id+"F9.opExtrude","SWEPT_EDGE",EDGE,{"disambiguationData":[OSD([subQ3,subQ2,subQ1,subQ0]),TDD([makeQuery(id+"F8.imprint","INTERSECT",VERTEX,{"disambiguationData":[OD(0.0)],"derivedFrom":[makeQuery(id+"F1.opExtrude","CAP_EDGE",EDGE,{"disambiguationData":[OSD([subQ3,subQ2])],"isStart":false}),subQ1,subQ0]})])]});}
            var Q8;
            {var subQ0=sQuery(id+"F10.wireOp",EDGE,"E65");var subQ1=sQuery(id+"F10.wireOp",EDGE,"E63");var subQ2=sQuery(id+"F4.wireOp",EDGE,"E34");Q8=makeQuery(id+"F11.opExtrude","SWEPT_EDGE",EDGE,{"disambiguationData":[OSD([subQ2,subQ1,subQ0]),TDD([makeQuery(id+"F10.imprint","INTERSECT",VERTEX,{"disambiguationData":[OD(0.0)],"derivedFrom":[makeQuery(id+"F5.opExtrude","CAP_EDGE",EDGE,{"disambiguationData":[OSD([subQ2])],"isStart":false}),subQ1,subQ0]})])]});}
            var Q9;
            {var subQ0=sQuery(id+"F10.wireOp",EDGE,"E68.MirrorCS");var subQ1=sQuery(id+"F10.wireOp",EDGE,"E67.MirrorCS");var subQ2=sQuery(id+"F4.wireOp",EDGE,"E34");Q9=makeQuery(id+"F11.opExtrude","SWEPT_EDGE",EDGE,{"disambiguationData":[OSD([subQ2,subQ1,subQ0]),TDD([makeQuery(id+"F10.imprint","INTERSECT",VERTEX,{"disambiguationData":[OD(1.0)],"derivedFrom":[makeQuery(id+"F5.opExtrude","CAP_EDGE",EDGE,{"disambiguationData":[OSD([subQ2])],"isStart":false}),subQ1,subQ0]})])]});}
            var Q10;
            {var subQ0=sQuery(id+"F10.wireOp",EDGE,"E68.MirrorCS");var subQ1=sQuery(id+"F10.wireOp",EDGE,"E67.MirrorCS");var subQ2=sQuery(id+"F4.wireOp",EDGE,"E34");Q10=makeQuery(id+"F11.opExtrude","SWEPT_EDGE",EDGE,{"disambiguationData":[OSD([subQ2,subQ1,subQ0]),TDD([makeQuery(id+"F10.imprint","INTERSECT",VERTEX,{"disambiguationData":[OD(0.0)],"derivedFrom":[makeQuery(id+"F5.opExtrude","CAP_EDGE",EDGE,{"disambiguationData":[OSD([subQ2])],"isStart":false}),subQ1,subQ0]})])]});}
            var Q11;
            {var subQ0=sQuery(id+"F10.wireOp",EDGE,"E65");var subQ1=sQuery(id+"F10.wireOp",EDGE,"E63");var subQ2=sQuery(id+"F4.wireOp",EDGE,"E34");Q11=makeQuery(id+"F11.opExtrude","SWEPT_EDGE",EDGE,{"disambiguationData":[OSD([subQ2,subQ1,subQ0]),TDD([makeQuery(id+"F10.imprint","INTERSECT",VERTEX,{"disambiguationData":[OD(1.0)],"derivedFrom":[makeQuery(id+"F5.opExtrude","CAP_EDGE",EDGE,{"disambiguationData":[OSD([subQ2])],"isStart":false}),subQ1,subQ0]})])]});}
            var Q12;
            {var subQ0=sQuery(id+"F10.wireOp",EDGE,"E70.MirrorCS");var subQ1=sQuery(id+"F10.wireOp",EDGE,"E69.MirrorCS");var subQ2=sQuery(id+"F4.wireOp",EDGE,"E40");Q12=makeQuery(id+"F11.opExtrude","SWEPT_EDGE",EDGE,{"disambiguationData":[OSD([subQ2,subQ1,subQ0]),TDD([makeQuery(id+"F10.imprint","INTERSECT",VERTEX,{"disambiguationData":[OD(1.0)],"derivedFrom":[makeQuery(id+"F5.opExtrude","CAP_EDGE",EDGE,{"disambiguationData":[OSD([subQ2])],"isStart":false}),subQ1,subQ0]})])]});}
            var Q13;
            {var subQ0=sQuery(id+"F10.wireOp",EDGE,"E66");var subQ1=sQuery(id+"F10.wireOp",EDGE,"E64");var subQ2=sQuery(id+"F4.wireOp",EDGE,"E40");Q13=makeQuery(id+"F11.opExtrude","SWEPT_EDGE",EDGE,{"disambiguationData":[OSD([subQ2,subQ1,subQ0]),TDD([makeQuery(id+"F10.imprint","INTERSECT",VERTEX,{"disambiguationData":[OD(1.0)],"derivedFrom":[makeQuery(id+"F5.opExtrude","CAP_EDGE",EDGE,{"disambiguationData":[OSD([subQ2])],"isStart":false}),subQ1,subQ0]})])]});}
            var Q14;
            {var subQ0=sQuery(id+"F10.wireOp",EDGE,"E70.MirrorCS");var subQ1=sQuery(id+"F10.wireOp",EDGE,"E69.MirrorCS");var subQ2=sQuery(id+"F4.wireOp",EDGE,"E40");Q14=makeQuery(id+"F11.opExtrude","SWEPT_EDGE",EDGE,{"disambiguationData":[OSD([subQ2,subQ1,subQ0]),TDD([makeQuery(id+"F10.imprint","INTERSECT",VERTEX,{"disambiguationData":[OD(0.0)],"derivedFrom":[makeQuery(id+"F5.opExtrude","CAP_EDGE",EDGE,{"disambiguationData":[OSD([subQ2])],"isStart":false}),subQ1,subQ0]})])]});}
            var Q15;
            {var subQ0=sQuery(id+"F10.wireOp",EDGE,"E66");var subQ1=sQuery(id+"F10.wireOp",EDGE,"E64");var subQ2=sQuery(id+"F4.wireOp",EDGE,"E40");Q15=makeQuery(id+"F11.opExtrude","SWEPT_EDGE",EDGE,{"disambiguationData":[OSD([subQ2,subQ1,subQ0]),TDD([makeQuery(id+"F10.imprint","INTERSECT",VERTEX,{"disambiguationData":[OD(0.0)],"derivedFrom":[makeQuery(id+"F5.opExtrude","CAP_EDGE",EDGE,{"disambiguationData":[OSD([subQ2])],"isStart":false}),subQ1,subQ0]})])]});}
            var Q16;
            {var subQ0=sQuery(id+"F10.wireOp",EDGE,"E73");var subQ1=sQuery(id+"F10.wireOp",EDGE,"E71");var subQ2=sQuery(id+"F4.wireOp",EDGE,"E40");Q16=makeQuery(id+"F11.opExtrude","SWEPT_EDGE",EDGE,{"disambiguationData":[OSD([subQ2,subQ1,subQ0]),TDD([makeQuery(id+"F10.imprint","INTERSECT",VERTEX,{"disambiguationData":[OD(1.0)],"derivedFrom":[makeQuery(id+"F5.opExtrude","CAP_EDGE",EDGE,{"disambiguationData":[OSD([subQ2])],"isStart":false}),subQ1,subQ0]})])]});}
            var Q17;
            {var subQ0=sQuery(id+"F8.wireOp",EDGE,"E61");var subQ1=sQuery(id+"F8.wireOp",EDGE,"E59");var subQ2=sQuery(id+"F0.wireOp",EDGE,"E6.MirrorCS");var subQ3=sQuery(id+"F0.wireOp",EDGE,"E0");Q17=makeQuery(id+"F9.opExtrude","SWEPT_EDGE",EDGE,{"disambiguationData":[OSD([subQ3,subQ2,subQ1,subQ0]),TDD([makeQuery(id+"F8.imprint","INTERSECT",VERTEX,{"disambiguationData":[OD(0.0)],"derivedFrom":[makeQuery(id+"F1.opExtrude","CAP_EDGE",EDGE,{"disambiguationData":[OSD([subQ3,subQ2])],"isStart":false}),subQ1,subQ0]})])]});}
            var Q18;
            {var subQ0=sQuery(id+"F8.wireOp",EDGE,"E61");var subQ1=sQuery(id+"F8.wireOp",EDGE,"E59");var subQ2=sQuery(id+"F0.wireOp",EDGE,"E6.MirrorCS");var subQ3=sQuery(id+"F0.wireOp",EDGE,"E0");Q18=makeQuery(id+"F9.opExtrude","SWEPT_EDGE",EDGE,{"disambiguationData":[OSD([subQ3,subQ2,subQ1,subQ0]),TDD([makeQuery(id+"F8.imprint","INTERSECT",VERTEX,{"disambiguationData":[OD(1.0)],"derivedFrom":[makeQuery(id+"F1.opExtrude","CAP_EDGE",EDGE,{"disambiguationData":[OSD([subQ3,subQ2])],"isStart":false}),subQ1,subQ0]})])]});}
            var Q19;
            {var subQ0=sQuery(id+"F10.wireOp",EDGE,"E73");var subQ1=sQuery(id+"F10.wireOp",EDGE,"E71");var subQ2=sQuery(id+"F4.wireOp",EDGE,"E40");Q19=makeQuery(id+"F11.opExtrude","SWEPT_EDGE",EDGE,{"disambiguationData":[OSD([subQ2,subQ1,subQ0]),TDD([makeQuery(id+"F10.imprint","INTERSECT",VERTEX,{"disambiguationData":[OD(0.0)],"derivedFrom":[makeQuery(id+"F5.opExtrude","CAP_EDGE",EDGE,{"disambiguationData":[OSD([subQ2])],"isStart":false}),subQ1,subQ0]})])]});}
            var Q20;
            {var subQ0=sQuery(id+"F10.wireOp",EDGE,"E74");var subQ1=sQuery(id+"F10.wireOp",EDGE,"E72");var subQ2=sQuery(id+"F4.wireOp",EDGE,"E34");Q20=makeQuery(id+"F11.opExtrude","SWEPT_EDGE",EDGE,{"disambiguationData":[OSD([subQ2,subQ1,subQ0]),TDD([makeQuery(id+"F10.imprint","INTERSECT",VERTEX,{"disambiguationData":[OD(0.0)],"derivedFrom":[makeQuery(id+"F5.opExtrude","CAP_EDGE",EDGE,{"disambiguationData":[OSD([subQ2])],"isStart":false}),subQ1,subQ0]})])]});}
            var Q21;
            {var subQ0=sQuery(id+"F8.wireOp",EDGE,"E62");var subQ1=sQuery(id+"F8.wireOp",EDGE,"E60");var subQ2=sQuery(id+"F0.wireOp",EDGE,"E10.MirrorCS");var subQ3=sQuery(id+"F0.wireOp",EDGE,"E9.MirrorCS");Q21=makeQuery(id+"F9.opExtrude","SWEPT_EDGE",EDGE,{"disambiguationData":[OSD([subQ3,subQ2,subQ1,subQ0]),TDD([makeQuery(id+"F8.imprint","INTERSECT",VERTEX,{"disambiguationData":[OD(1.0)],"derivedFrom":[makeQuery(id+"F1.opExtrude","CAP_EDGE",EDGE,{"disambiguationData":[OSD([subQ3,subQ2])],"isStart":false}),subQ1,subQ0]})])]});}
            var Q22;
            {var subQ0=sQuery(id+"F10.wireOp",EDGE,"E74");var subQ1=sQuery(id+"F10.wireOp",EDGE,"E72");var subQ2=sQuery(id+"F4.wireOp",EDGE,"E34");Q22=makeQuery(id+"F11.opExtrude","SWEPT_EDGE",EDGE,{"disambiguationData":[OSD([subQ2,subQ1,subQ0]),TDD([makeQuery(id+"F10.imprint","INTERSECT",VERTEX,{"disambiguationData":[OD(1.0)],"derivedFrom":[makeQuery(id+"F5.opExtrude","CAP_EDGE",EDGE,{"disambiguationData":[OSD([subQ2])],"isStart":false}),subQ1,subQ0]})])]});}
            var Q23;
            {var subQ0=sQuery(id+"F8.wireOp",EDGE,"E62");var subQ1=sQuery(id+"F8.wireOp",EDGE,"E60");var subQ2=sQuery(id+"F0.wireOp",EDGE,"E10.MirrorCS");var subQ3=sQuery(id+"F0.wireOp",EDGE,"E9.MirrorCS");Q23=makeQuery(id+"F9.opExtrude","SWEPT_EDGE",EDGE,{"disambiguationData":[OSD([subQ3,subQ2,subQ1,subQ0]),TDD([makeQuery(id+"F8.imprint","INTERSECT",VERTEX,{"disambiguationData":[OD(0.0)],"derivedFrom":[makeQuery(id+"F1.opExtrude","CAP_EDGE",EDGE,{"disambiguationData":[OSD([subQ3,subQ2])],"isStart":false}),subQ1,subQ0]})])]});}
            fillet(context, id + "F19", {"entities" : qUnion([Q0, Q1, Q2, Q3, Q4, Q5, Q6, Q7, Q8, Q9, Q10, Q11, Q12, Q13, Q14, Q15, Q16, Q17, Q18, Q19, Q20, Q21, Q22, Q23]), "radius" : 3.5 * mm, "tangentPropagation" : true, "allowEdgeOverflow" : false});
        }
        {
            var Q0;
            Q0=makeQuery(id+"F5.opExtrude","SWEPT_EDGE",EDGE,{"disambiguationData":[OSD([sQuery(id+"F4.wireOp",EDGE,"E39"),sQuery(id+"F4.wireOp",EDGE,"E40")])]});
            var Q1;
            Q1=makeQuery(id+"F5.opExtrude","SWEPT_EDGE",EDGE,{"disambiguationData":[OSD([sQuery(id+"F4.wireOp",EDGE,"E34"),sQuery(id+"F4.wireOp",EDGE,"E36")])]});
            var Q2;
            Q2=makeQuery(id+"F5.opExtrude","SWEPT_EDGE",EDGE,{"disambiguationData":[OSD([sQuery(id+"F4.wireOp",EDGE,"E40"),sQuery(id+"F4.wireOp",EDGE,"E41")])]});
            var Q3;
            Q3=makeQuery(id+"F5.opExtrude","SWEPT_EDGE",EDGE,{"disambiguationData":[OSD([sQuery(id+"F4.wireOp",EDGE,"E34"),sQuery(id+"F4.wireOp",EDGE,"E38.MirrorCS")])]});
            var Q4;
            Q4=makeQuery(id+"F1.opExtrude","SWEPT_EDGE",EDGE,{"disambiguationData":[OSD([sQuery(id+"F0.wireOp",EDGE,"E0"),sQuery(id+"F0.wireOp",EDGE,"E4")])]});
            var Q5;
            Q5=makeQuery(id+"F1.opExtrude","SWEPT_EDGE",EDGE,{"disambiguationData":[OSD([sQuery(id+"F0.wireOp",EDGE,"E8.MirrorCS"),sQuery(id+"F0.wireOp",EDGE,"E9.MirrorCS")])]});
            var Q6;
            Q6=makeQuery(id+"F5.opExtrude","SWEPT_EDGE",EDGE,{"disambiguationData":[OSD([sQuery(id+"F4.wireOp",EDGE,"86d8c83e-cf90-450f-aea3-c100bfa3c6ad0.MirrorCS"),sQuery(id+"F4.wireOp",EDGE,"E41")])]});
            var Q7;
            Q7=makeQuery(id+"F5.opExtrude","SWEPT_EDGE",EDGE,{"disambiguationData":[OSD([sQuery(id+"F4.wireOp",EDGE,"E37.MirrorCS"),sQuery(id+"F4.wireOp",EDGE,"E38.MirrorCS")])]});
            var Q8;
            Q8=makeQuery(id+"F7.opExtrude","SWEPT_EDGE",EDGE,{"disambiguationData":[OSD([sQuery(id+"F4.wireOp",EDGE,"E34"),sQuery(id+"F4.wireOp",EDGE,"E38.MirrorCS"),sQuery(id+"F6.wireOp",EDGE,"E49"),sQuery(id+"F6.wireOp",EDGE,"E50")])]});
            var Q9;
            Q9=makeQuery(id+"F1.opExtrude","SWEPT_EDGE",EDGE,{"disambiguationData":[OSD([sQuery(id+"F0.wireOp",EDGE,"E2"),sQuery(id+"F0.wireOp",EDGE,"E4")])]});
            var Q10;
            Q10=makeQuery(id+"F3.opExtrude","SWEPT_EDGE",EDGE,{"disambiguationData":[OSD([sQuery(id+"F0.wireOp",EDGE,"E8.MirrorCS"),sQuery(id+"F0.wireOp",EDGE,"E9.MirrorCS"),sQuery(id+"F2.wireOp",EDGE,"E26"),sQuery(id+"F2.wireOp",EDGE,"E27")])]});
            var Q11;
            Q11=makeQuery(id+"F1.opExtrude","SWEPT_EDGE",EDGE,{"disambiguationData":[OSD([sQuery(id+"F0.wireOp",EDGE,"E8.MirrorCS"),sQuery(id+"F0.wireOp",EDGE,"E16.MirrorCS")])]});
            var Q12;
            Q12=makeQuery(id+"F1.opExtrude","SWEPT_EDGE",EDGE,{"disambiguationData":[OSD([sQuery(id+"F0.wireOp",EDGE,"E10.MirrorCS"),sQuery(id+"F0.wireOp",EDGE,"E11.MirrorCS")])]});
            var Q13;
            Q13=makeQuery(id+"F1.opExtrude","SWEPT_EDGE",EDGE,{"disambiguationData":[OSD([sQuery(id+"F0.wireOp",EDGE,"E6.MirrorCS"),sQuery(id+"F0.wireOp",EDGE,"E7.MirrorCS")])]});
            var Q14;
            Q14=makeQuery(id+"F1.opExtrude","SWEPT_EDGE",EDGE,{"disambiguationData":[OSD([sQuery(id+"F0.wireOp",EDGE,"E7.MirrorCS"),sQuery(id+"F0.wireOp",EDGE,"E15.MirrorCS")])]});
            var Q15;
            Q15=makeQuery(id+"F5.opExtrude","SWEPT_EDGE",EDGE,{"disambiguationData":[OSD([sQuery(id+"F4.wireOp",EDGE,"85350aae-0de3-47d0-8ac1-9a2e1902549b0.MirrorCS"),sQuery(id+"F4.wireOp",EDGE,"E39")])]});
            var Q16;
            Q16=makeQuery(id+"F7.opExtrude","SWEPT_EDGE",EDGE,{"disambiguationData":[OSD([sQuery(id+"F4.wireOp",EDGE,"E34"),sQuery(id+"F4.wireOp",EDGE,"E36"),sQuery(id+"F6.wireOp",EDGE,"E47"),sQuery(id+"F6.wireOp",EDGE,"E50")])]});
            var Q17;
            Q17=makeQuery(id+"F3.opExtrude","SWEPT_EDGE",EDGE,{"disambiguationData":[OSD([sQuery(id+"F0.wireOp",EDGE,"E10.MirrorCS"),sQuery(id+"F0.wireOp",EDGE,"E11.MirrorCS"),sQuery(id+"F2.wireOp",EDGE,"E31.MirrorCS"),sQuery(id+"F2.wireOp",EDGE,"E32.MirrorCS")])]});
            var Q18;
            Q18=makeQuery(id+"F1.opExtrude","SWEPT_EDGE",EDGE,{"disambiguationData":[OSD([sQuery(id+"F0.wireOp",EDGE,"E11.MirrorCS"),sQuery(id+"F0.wireOp",EDGE,"E19.MirrorCS")])]});
            var Q19;
            Q19=makeQuery(id+"F5.opExtrude","SWEPT_EDGE",EDGE,{"disambiguationData":[OSD([sQuery(id+"F4.wireOp",EDGE,"E35"),sQuery(id+"F4.wireOp",EDGE,"E36")])]});
            var Q20;
            Q20=makeQuery(id+"F7.boolean.opBoolean","INTERSECT",EDGE,{"derivedFrom":[makeQuery(id+"F5.opExtrude","SWEPT_FACE",FACE,{"disambiguationData":[OSD([sQuery(id+"F4.wireOp",EDGE,"E33")])]}),makeQuery(id+"F7.opExtrude","SWEPT_FACE",FACE,{"disambiguationData":[OSD([sQuery(id+"F6.wireOp",EDGE,"E50")])]})]});
            var Q21;
            Q21=makeQuery(id+"F7.boolean.opBoolean","INTERSECT",EDGE,{"derivedFrom":[makeQuery(id+"F5.opExtrude","SWEPT_FACE",FACE,{"disambiguationData":[OSD([sQuery(id+"F4.wireOp",EDGE,"E43.MirrorCS")])]}),makeQuery(id+"F7.opExtrude","SWEPT_FACE",FACE,{"disambiguationData":[OSD([sQuery(id+"F6.wireOp",EDGE,"E50")])]})]});
            var Q22;
            Q22=makeQuery(id+"F5.opExtrude","CAP_EDGE",EDGE,{"disambiguationData":[OSD([sQuery(id+"F4.wireOp",EDGE,"E33")])],"isStart":true});
            var Q23;
            Q23=makeQuery(id+"F5.opExtrude","CAP_EDGE",EDGE,{"disambiguationData":[OSD([sQuery(id+"F4.wireOp",EDGE,"E43.MirrorCS")])],"isStart":true});
            fillet(context, id + "F20", {"entities" : qUnion([Q0, Q1, Q2, Q3, Q4, Q5, Q6, Q7, Q8, Q9, Q10, Q11, Q12, Q13, Q14, Q15, Q16, Q17, Q18, Q19, Q20, Q21, Q22, Q23]), "radius" : 1 * mm, "tangentPropagation" : true, "allowEdgeOverflow" : false});
        }
        {
            var Q0;
            Q0=makeQuery(id+"F9.boolean.opBoolean","MERGE",FACE,{"derivedFrom":[makeQuery(id+"F3.boolean.opBoolean","MERGE",FACE,{"derivedFrom":[makeQuery(id+"F1.opExtrude","CAP_FACE",FACE,{"disambiguationData":[OSD([sQuery(id+"F0.wireOp",EDGE,"E0"),sQuery(id+"F0.wireOp",EDGE,"E2"),sQuery(id+"F0.wireOp",EDGE,"E4"),sQuery(id+"F0.wireOp",EDGE,"E6.MirrorCS"),sQuery(id+"F0.wireOp",EDGE,"E7.MirrorCS"),sQuery(id+"F0.wireOp",EDGE,"E13"),sQuery(id+"F0.wireOp",EDGE,"E14.MirrorCS"),sQuery(id+"F0.wireOp",EDGE,"E15.MirrorCS")])],"isStart":false}),makeQuery(id+"F1.opExtrude","CAP_FACE",FACE,{"disambiguationData":[OSD([sQuery(id+"F0.wireOp",EDGE,"E8.MirrorCS"),sQuery(id+"F0.wireOp",EDGE,"E9.MirrorCS"),sQuery(id+"F0.wireOp",EDGE,"E10.MirrorCS"),sQuery(id+"F0.wireOp",EDGE,"E11.MirrorCS"),sQuery(id+"F0.wireOp",EDGE,"E16.MirrorCS"),sQuery(id+"F0.wireOp",EDGE,"E17.MirrorCS"),sQuery(id+"F0.wireOp",EDGE,"E18.MirrorCS"),sQuery(id+"F0.wireOp",EDGE,"E19.MirrorCS")])],"isStart":false}),makeQuery(id+"F3.opExtrude","SWEPT_FACE",FACE,{"disambiguationData":[OSD([sQuery(id+"F2.wireOp",EDGE,"E25"),sQuery(id+"F2.wireOp",EDGE,"E30.MirrorCS")])]})]}),makeQuery(id+"F9.opExtrude","CAP_FACE",FACE,{"disambiguationData":[OSD([sQuery(id+"F8.wireOp",EDGE,"E51"),sQuery(id+"F8.wireOp",EDGE,"E53")])],"isStart":true}),makeQuery(id+"F9.opExtrude","CAP_FACE",FACE,{"disambiguationData":[OSD([sQuery(id+"F8.wireOp",EDGE,"E52"),sQuery(id+"F8.wireOp",EDGE,"E54")])],"isStart":true}),makeQuery(id+"F9.opExtrude","CAP_FACE",FACE,{"disambiguationData":[OSD([sQuery(id+"F8.wireOp",EDGE,"E55.MirrorCS"),sQuery(id+"F8.wireOp",EDGE,"E58.MirrorCS")])],"isStart":true}),makeQuery(id+"F9.opExtrude","CAP_FACE",FACE,{"disambiguationData":[OSD([sQuery(id+"F8.wireOp",EDGE,"E56.MirrorCS"),sQuery(id+"F8.wireOp",EDGE,"E57.MirrorCS")])],"isStart":true}),makeQuery(id+"F9.opExtrude","CAP_FACE",FACE,{"disambiguationData":[OSD([sQuery(id+"F8.wireOp",EDGE,"E59"),sQuery(id+"F8.wireOp",EDGE,"E61")])],"isStart":true}),makeQuery(id+"F9.opExtrude","CAP_FACE",FACE,{"disambiguationData":[OSD([sQuery(id+"F8.wireOp",EDGE,"E60"),sQuery(id+"F8.wireOp",EDGE,"E62")])],"isStart":true})]});
            var Q1;
            Q1=makeQuery(id+"F11.boolean.opBoolean","MERGE",FACE,{"derivedFrom":[makeQuery(id+"F7.boolean.opBoolean","MERGE",FACE,{"derivedFrom":[makeQuery(id+"F5.opExtrude","CAP_FACE",FACE,{"disambiguationData":[OSD([sQuery(id+"F4.wireOp",EDGE,"E33"),sQuery(id+"F4.wireOp",EDGE,"E34"),sQuery(id+"F4.wireOp",EDGE,"E35"),sQuery(id+"F4.wireOp",EDGE,"E36"),sQuery(id+"F4.wireOp",EDGE,"E37.MirrorCS"),sQuery(id+"F4.wireOp",EDGE,"E38.MirrorCS")])],"isStart":false}),makeQuery(id+"F5.opExtrude","CAP_FACE",FACE,{"disambiguationData":[OSD([sQuery(id+"F4.wireOp",EDGE,"E39"),sQuery(id+"F4.wireOp",EDGE,"E40"),sQuery(id+"F4.wireOp",EDGE,"E41"),sQuery(id+"F4.wireOp",EDGE,"E42.MirrorCS"),sQuery(id+"F4.wireOp",EDGE,"E43.MirrorCS"),sQuery(id+"F4.wireOp",EDGE,"E44.MirrorCS")])],"isStart":false}),makeQuery(id+"F7.opExtrude","SWEPT_FACE",FACE,{"disambiguationData":[OSD([sQuery(id+"F6.wireOp",EDGE,"E48")])]})]}),makeQuery(id+"F11.opExtrude","CAP_FACE",FACE,{"disambiguationData":[OSD([sQuery(id+"F10.wireOp",EDGE,"E63"),sQuery(id+"F10.wireOp",EDGE,"E65")])],"isStart":true}),makeQuery(id+"F11.opExtrude","CAP_FACE",FACE,{"disambiguationData":[OSD([sQuery(id+"F10.wireOp",EDGE,"E64"),sQuery(id+"F10.wireOp",EDGE,"E66")])],"isStart":true}),makeQuery(id+"F11.opExtrude","CAP_FACE",FACE,{"disambiguationData":[OSD([sQuery(id+"F10.wireOp",EDGE,"E67.MirrorCS"),sQuery(id+"F10.wireOp",EDGE,"E68.MirrorCS")])],"isStart":true}),makeQuery(id+"F11.opExtrude","CAP_FACE",FACE,{"disambiguationData":[OSD([sQuery(id+"F10.wireOp",EDGE,"E69.MirrorCS"),sQuery(id+"F10.wireOp",EDGE,"E70.MirrorCS")])],"isStart":true}),makeQuery(id+"F11.opExtrude","CAP_FACE",FACE,{"disambiguationData":[OSD([sQuery(id+"F10.wireOp",EDGE,"E71"),sQuery(id+"F10.wireOp",EDGE,"E73")])],"isStart":true}),makeQuery(id+"F11.opExtrude","CAP_FACE",FACE,{"disambiguationData":[OSD([sQuery(id+"F10.wireOp",EDGE,"E72"),sQuery(id+"F10.wireOp",EDGE,"E74")])],"isStart":true})]});
            fillet(context, id + "F21", {"entities" : qUnion([Q0, Q1]), "radius" : 0.5 * mm, "tangentPropagation" : true, "allowEdgeOverflow" : false});
        }
    });
